# Revit family: 820-10-032-DN350-600
name_source: partatom
category: Pipe Accessories
units: mm (PartAtom-declared; Revit-internal decimal feet)

## family parameters
Always vertical = Yes
Cut with Voids When Loaded = No
Part Type = Valve - Breaks Into
Round Connector Dimension = Use Diameter
Shared = No
Work Plane-Based = No

## types (10) — shared parameters
3 = 3 mm  [stored 0.00984252 ft]
Body_wallthickness = 10 mm  [stored 0.0328084 ft]
DN350_PN10 = 820-0350-10-04010030002
DN350_PN16 = 820-0350-10-04010160002
DN400_PN10 = 820-0400-10-04010030002
DN400_PN16 = 820-0400-10-04010160002
DN450_PN10 = 820-0450-10-04040031002
DN450_PN16 = 820-0450-10-04040161002
DN500_PN10 = 820-0500-10-04040031002
DN500_PN16 = 820-0500-10-04040161002
DN600_PN10 = 820-0600-10-04040031002
DN600_PN16 = 820-0600-10-04040161002
Description_ = AVK CENTRIC BUTTERFLY VALVE LUG TYPE, PN10/16
Flange_thickness = 10 mm  [stored 0.0328084 ft]
Search_table = 820-10-032-DN350-600
URL product pages = https://www.avkvalves.com
fillet = 20 mm  [stored 0.0656168 ft]
zero-valued in all types: Default Elevation

## per-type parameters (varying)
| type | Actuator_Dia | Bore | DN | EPDM | F | F2 | H2 | Hole_dia | ID | L | L2 | L_ref | L_ref_2 | L_ref_3 | Lug_D | Lug_D1 | PCD | Rubber_r | W2_ref |
| DN350_PN10 | 150 mm | 175 mm | 350 mm | 173 mm | 22 mm  [stored 0.0721785 ft] | 40 mm  [stored 0.131234 ft] | 258 mm | 37 mm  [stored 0.121391 ft] | 175 mm | 80 mm  [stored 0.262467 ft] | 260 mm | 60 mm  [stored 0.19685 ft] | 120 mm  [stored 0.393701 ft] | 50 mm  [stored 0.164042 ft] | 30 mm  [stored 0.0984252 ft] | 53 mm  [stored 0.173885 ft] | 230 mm | 180 mm | 330 mm |
| DN350_PN16 | 150 mm | 175 mm | 350 mm | 173 mm | 22 mm  [stored 0.0721785 ft] | 40 mm  [stored 0.131234 ft] | 258 mm | 37 mm  [stored 0.121391 ft] | 175 mm | 80 mm  [stored 0.262467 ft] | 260 mm | 60 mm  [stored 0.19685 ft] | 120 mm  [stored 0.393701 ft] | 50 mm  [stored 0.164042 ft] | 25 mm  [stored 0.082021 ft] | 44 mm  [stored 0.144357 ft] | 235 mm | 180 mm | 330 mm |
| DN400_PN10 | 150 mm | 200 mm | 400 mm | 198 mm | 27 mm  [stored 0.0885827 ft] | 40 mm  [stored 0.131234 ft] | 290 mm | 41 mm  [stored 0.134514 ft] | 200 mm | 102 mm  [stored 0.334646 ft] | 292 mm | 82 mm  [stored 0.269029 ft] | 164 mm | 68 mm | 35 mm  [stored 0.114829 ft] | 60 mm  [stored 0.19685 ft] | 258 mm | 205 mm | 365 mm |
| DN400_PN16 | 150 mm | 200 mm | 400 mm | 198 mm | 27 mm  [stored 0.0885827 ft] | 40 mm  [stored 0.131234 ft] | 290 mm | 41 mm  [stored 0.134514 ft] | 200 mm | 102 mm  [stored 0.334646 ft] | 292 mm | 82 mm  [stored 0.269029 ft] | 164 mm | 68 mm | 30 mm  [stored 0.0984252 ft] | 52 mm  [stored 0.170604 ft] | 263 mm | 205 mm | 365 mm |
| DN450_PN16 | 175 mm | 225 mm | 450 mm | 223 mm | 45 mm  [stored 0.147638 ft] | 65 mm  [stored 0.213255 ft] | 355 mm | 41 mm  [stored 0.134514 ft] | 225 mm | 113 mm  [stored 0.370735 ft] | 328 mm | 93 mm  [stored 0.305118 ft] | 186 mm | 78 mm | 35 mm  [stored 0.114829 ft] | 61 mm | 293 mm | 230 mm | 397 mm |
| DN450_PN10 | 175 mm | 225 mm | 450 mm | 223 mm | 45 mm  [stored 0.147638 ft] | 65 mm  [stored 0.213255 ft] | 355 mm | 41 mm  [stored 0.134514 ft] | 225 mm | 113 mm  [stored 0.370735 ft] | 328 mm | 93 mm  [stored 0.305118 ft] | 186 mm | 78 mm | 45 mm  [stored 0.147638 ft] | 79 mm | 283 mm | 230 mm | 397 mm |
| DN500_PN10 | 175 mm | 250 mm | 500 mm | 248 mm | 45 mm  [stored 0.147638 ft] | 65 mm  [stored 0.213255 ft] | 393 mm | 44 mm  [stored 0.144357 ft] | 250 mm | 126 mm  [stored 0.413386 ft] | 356 mm | 106 mm  [stored 0.347769 ft] | 212 mm | 88 mm | 46 mm  [stored 0.150919 ft] | 81 mm | 310 mm | 255 mm | 437 mm |
| DN500_PN16 | 175 mm | 250 mm | 500 mm | 248 mm | 45 mm  [stored 0.147638 ft] | 65 mm  [stored 0.213255 ft] | 393 mm | 44 mm  [stored 0.144357 ft] | 250 mm | 126 mm  [stored 0.413386 ft] | 356 mm | 106 mm  [stored 0.347769 ft] | 212 mm | 88 mm | 36 mm  [stored 0.11811 ft] | 63 mm  [stored 0.206693 ft] | 320 mm | 255 mm | 437 mm |
| DN600_PN10 | 210 mm | 300 mm | 600 mm | 298 mm | 70 mm  [stored 0.229659 ft] | 80 mm  [stored 0.262467 ft] | 464 mm | 50 mm  [stored 0.164042 ft] | 300 mm | 153 mm | 415 mm | 133 mm  [stored 0.436352 ft] | 266 mm | 111 mm | 52 mm  [stored 0.170604 ft] | 91 mm  [stored 0.298556 ft] | 363 mm | 305 mm | 522 mm |
| DN600_PN16 | 210 mm | 300 mm | 600 mm | 298 mm | 70 mm  [stored 0.229659 ft] | 80 mm  [stored 0.262467 ft] | 464 mm | 50 mm  [stored 0.164042 ft] | 300 mm | 153 mm | 415 mm | 133 mm  [stored 0.436352 ft] | 266 mm | 111 mm | 37 mm  [stored 0.121391 ft] | 65 mm  [stored 0.213255 ft] | 378 mm | 305 mm | 522 mm |

note: [stored X ft] marks values corroborated as IEEE doubles in the binary element streams (Revit-internal decimal feet)

## geometry (parser evidence)
native form markers: Sweep x5
no freeform markers — native parametric forms only
